# Revit family: Urbania_Patio_Door_OXXO
name_source: partatom
category: Doors
units: mm (PartAtom-declared; Revit-internal decimal feet)

## family parameters
Always vertical = Yes
Classification Number = 23.30.10.00
Cut with Voids When Loaded = No
Host = Wall
Room Calculation Point = No
Shared = No

## types (2) — shared parameters
6p vs 7.25p = No
Analytic Construction = <Aucun>
Define Thermal Properties by = Schematic Type
Door width O = 878 mm  [stored 2.88058 ft]
Door width X = 910 mm
Edge thickness = 25 mm  [stored 0.082021 ft]
FRAME TYPE = Urbania_Standar Frame_ 4 Panels_7.25'' : Patio_Frame_7.25p
Frame width = 75 mm  [stored 0.246063 ft]
Front panel distance = 83 mm
Function = Interior
Head height O = 19 mm  [stored 0.062336 ft]
Head height X = 22 mm  [stored 0.0721785 ft]
Height = 2057 mm
Manufacturer = Novatech Group
Model = Urbania/Loft 71/4p
Overlap = 42 mm  [stored 0.137795 ft]
Panel Profile O = 31 mm  [stored 0.101706 ft]
Panel Profile X = 63 mm  [stored 0.206693 ft]
Panel height  X = 1995 mm  [stored 6.54528 ft]
Panel height O = 2005 mm  [stored 6.57808 ft]
Projection - Exterior of frame = 25 mm  [stored 0.082021 ft]
Projection - Interior of frame = 25 mm  [stored 0.082021 ft]
Rough Height = 2070 mm
Rough Width = 3555 mm
Threshold height O side = 33 mm  [stored 0.108268 ft]
Threshold height X side = 40 mm  [stored 0.131234 ft]
URL = https://www.groupenovatech.com
Wall Closure = By host
Width = 3542 mm  [stored 11.6207 ft]

## type names (no varying parameters)
- Patio_Door_6p
- Patio_Door_7.25

note: [stored X ft] marks values corroborated as IEEE doubles in the binary element streams (Revit-internal decimal feet)
